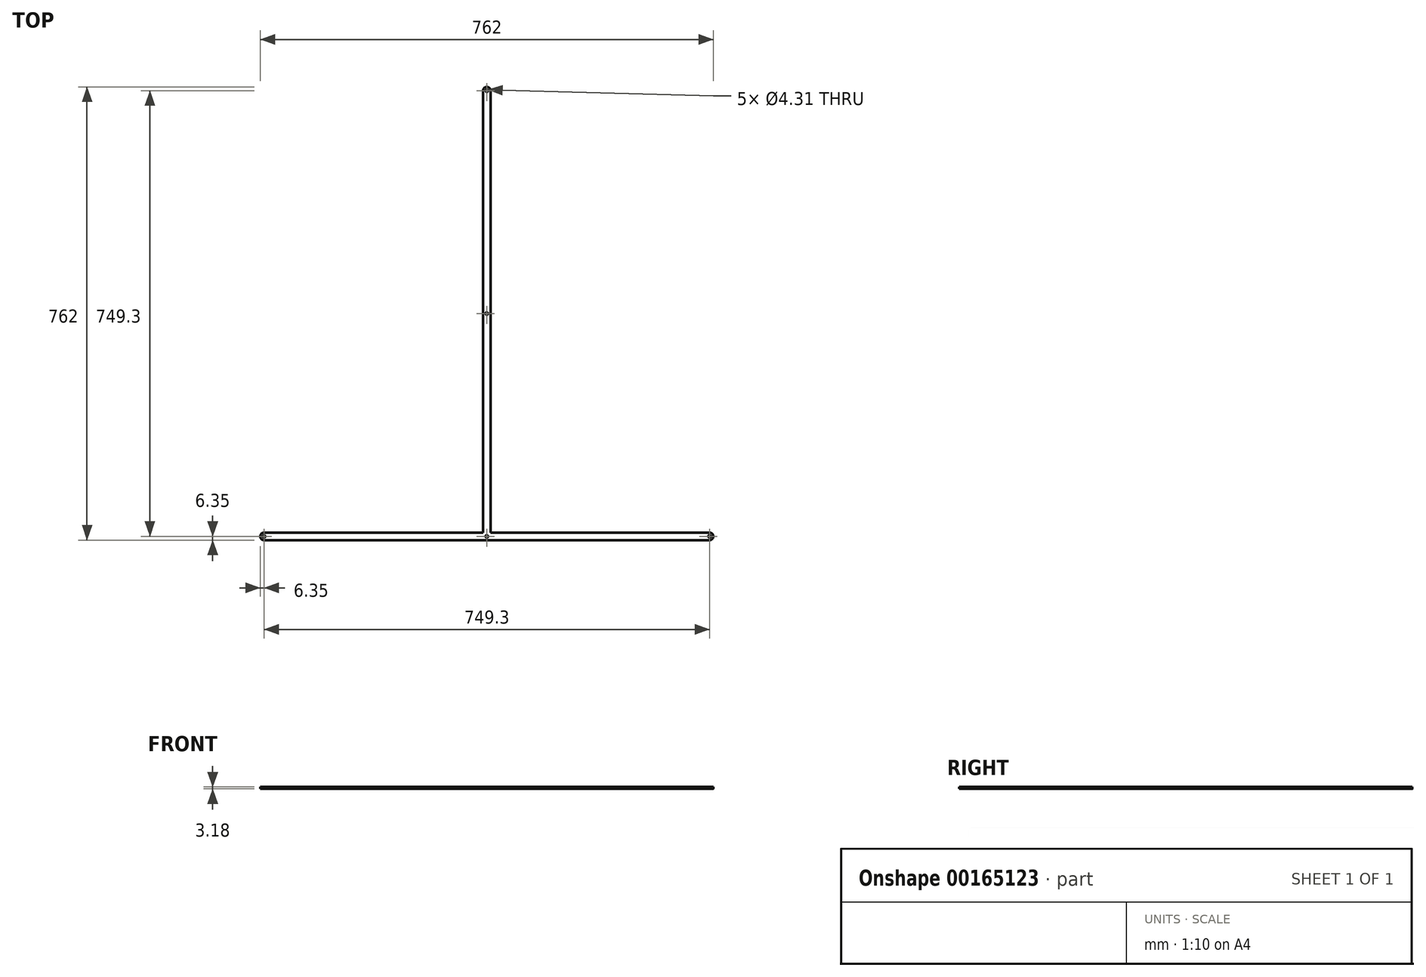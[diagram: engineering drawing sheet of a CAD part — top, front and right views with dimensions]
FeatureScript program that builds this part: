
annotation { "Feature Type Name" : "Feature", "Feature Type Description" : "" }
export const myFeature = defineFeature(function(context is Context, id is Id, definition is map)
    precondition{}
    {
        {
            var Q0;
            Q0=qCreatedBy(makeId("Top.planeOp"),FACE);
            var sketch = newSketch(context, id + "F0", { "sketchPlane" : qUnion([Q0])});
            skLineSegment(sketch, "E0.top", {"start": v(0, 749.3) * mm, "end": v(12.7, 749.3) * mm});
            skLineSegment(sketch, "E0.left", {"start": v(0, 0) * mm, "end": v(0, 749.3) * mm});
            skLineSegment(sketch, "E0.right", {"start": v(12.7, 0) * mm, "end": v(12.7, 749.3) * mm});
            skLineSegment(sketch, "E1", {"start": v(6.35, 749.3) * mm, "end": v(6.35, 742.95) * mm, "construction": true});
            skLineSegment(sketch, "E2", {"start": v(6.35, 742.95) * mm, "end": v(12.7, 742.95) * mm, "construction": true});
            skLineSegment(sketch, "E3", {"start": v(6.35, 742.95) * mm, "end": v(6.35, -6.35) * mm, "construction": true});
            skLineSegment(sketch, "E4", {"start": v(6.35, -6.35) * mm, "end": v(6.35, -12.7) * mm, "construction": true});
            skLineSegment(sketch, "E5.bottom", {"start": v(0, 0) * mm, "end": v(-374.65, 0) * mm});
            skLineSegment(sketch, "E5.top", {"start": v(387.35, -12.7) * mm, "end": v(-374.65, -12.7) * mm});
            skLineSegment(sketch, "E5.right", {"start": v(-374.65, 0) * mm, "end": v(-374.65, -12.7) * mm});
            skLineSegment(sketch, "E6.bottom", {"start": v(12.7, 0) * mm, "end": v(387.35, 0) * mm});
            skLineSegment(sketch, "E6.right", {"start": v(387.35, 0) * mm, "end": v(387.35, -12.7) * mm});
            skLineSegment(sketch, "E7", {"start": v(-374.65, -6.35) * mm, "end": v(-368.3, -6.35) * mm, "construction": true});
            skLineSegment(sketch, "E8", {"start": v(-368.3, -6.35) * mm, "end": v(381, -6.35) * mm, "construction": true});
            skLineSegment(sketch, "E9", {"start": v(381, -6.35) * mm, "end": v(387.35, -6.35) * mm, "construction": true});
            skCircle(sketch, "E10", {"center": v(6.35, 742.95) * mm, "radius": 2.15 * mm});
            skCircle(sketch, "E11", {"center": v(6.35, 368.3) * mm, "radius": 2.15 * mm});
            skCircle(sketch, "E12", {"center": v(381, -6.35) * mm, "radius": 2.15 * mm});
            skCircle(sketch, "E13", {"center": v(6.35, -6.35) * mm, "radius": 2.15 * mm});
            skCircle(sketch, "E14", {"center": v(-368.3, -6.35) * mm, "radius": 2.15 * mm});
            skSolve(sketch);
        }
        {
            var Q0;
            Q0 = qSketchRegion(id + "F0", true);
            extrude(context, id + "F1", {"entities" : qUnion([Q0]), "depth" : 3.17 * mm});
        }
        {
            var Q0;
            Q0=makeQuery(id+"F1.opExtrude","SWEPT_EDGE",EDGE,{"disambiguationData":[OSD([sQuery(id+"F0.wireOp",EDGE,"E0.top"),sQuery(id+"F0.wireOp",EDGE,"E0.left")])]});
            var Q1;
            Q1=makeQuery(id+"F1.opExtrude","SWEPT_EDGE",EDGE,{"disambiguationData":[OSD([sQuery(id+"F0.wireOp",EDGE,"E0.top"),sQuery(id+"F0.wireOp",EDGE,"E0.right")])]});
            var Q2;
            Q2=makeQuery(id+"F1.opExtrude","SWEPT_EDGE",EDGE,{"disambiguationData":[OSD([sQuery(id+"F0.wireOp",EDGE,"E5.top"),sQuery(id+"F0.wireOp",EDGE,"E6.right")])]});
            var Q3;
            Q3=makeQuery(id+"F1.opExtrude","SWEPT_EDGE",EDGE,{"disambiguationData":[OSD([sQuery(id+"F0.wireOp",EDGE,"E6.bottom"),sQuery(id+"F0.wireOp",EDGE,"E6.right")])]});
            var Q4;
            Q4=makeQuery(id+"F1.opExtrude","SWEPT_EDGE",EDGE,{"disambiguationData":[OSD([sQuery(id+"F0.wireOp",EDGE,"E5.top"),sQuery(id+"F0.wireOp",EDGE,"E5.right")])]});
            var Q5;
            Q5=makeQuery(id+"F1.opExtrude","SWEPT_EDGE",EDGE,{"disambiguationData":[OSD([sQuery(id+"F0.wireOp",EDGE,"E5.bottom"),sQuery(id+"F0.wireOp",EDGE,"E5.right")])]});
            fillet(context, id + "F2", {"entities" : qUnion([Q0, Q1, Q2, Q3, Q4, Q5]), "radius" : 6.35 * mm, "tangentPropagation" : true, "allowEdgeOverflow" : false});
        }
    });
